# Revit family: P4100SL
name_source: partatom
category: Generic Models
units: mm (PartAtom-declared; Revit-internal decimal feet)

## family parameters
Can host rebar = No
Cut with Voids When Loaded = No
Part Type = Normal
Room Calculation Point = No
Round Connector Dimension = Use Diameter
Shared = No

## types (5) — shared parameters
Description = P4100SL - 1-5/8" x 13/16", 14 Gauge, Long Slots - GenericModels
Height = 0.813"
Manufacturer = Atkore Unistrut
Model = P4100SL
Salsify ID1 = US-P4100SL
URL = https://www.atkore.com
zero-valued in all types: Default Elevation

## per-type parameters (varying)
| type | Material | Power-Strut Part Number | UPC-10ft | UPC-20ft | Unit Weight |
| P4100SL PG | Pre-Galvanized | PS 500 S PGAL | "0786364893334" | "786364893358" | 0.97 lb/ft |
| P4100SL ZD | Zinc Dichromate | PS 500 S ZD | "0" | "0" | 0.87 lb/ft |
| P4100SL HG | Hot Dip Galvanized | PS 500 S HDG | "0786364062075" | "0" | 0.87 lb/ft |
| P4100SL GR | Green | PS 500 S GRN | "0786364893327" | "786364893341" | 0.97 lb/ft |
| P4100SL PL | Plain |  | "0" | "0" | 0.97 lb/ft |

note: column(s) folded — value = type name in every type: Part Number

## geometry (parser evidence)
native form markers: Sweep x9
no freeform markers — native parametric forms only
